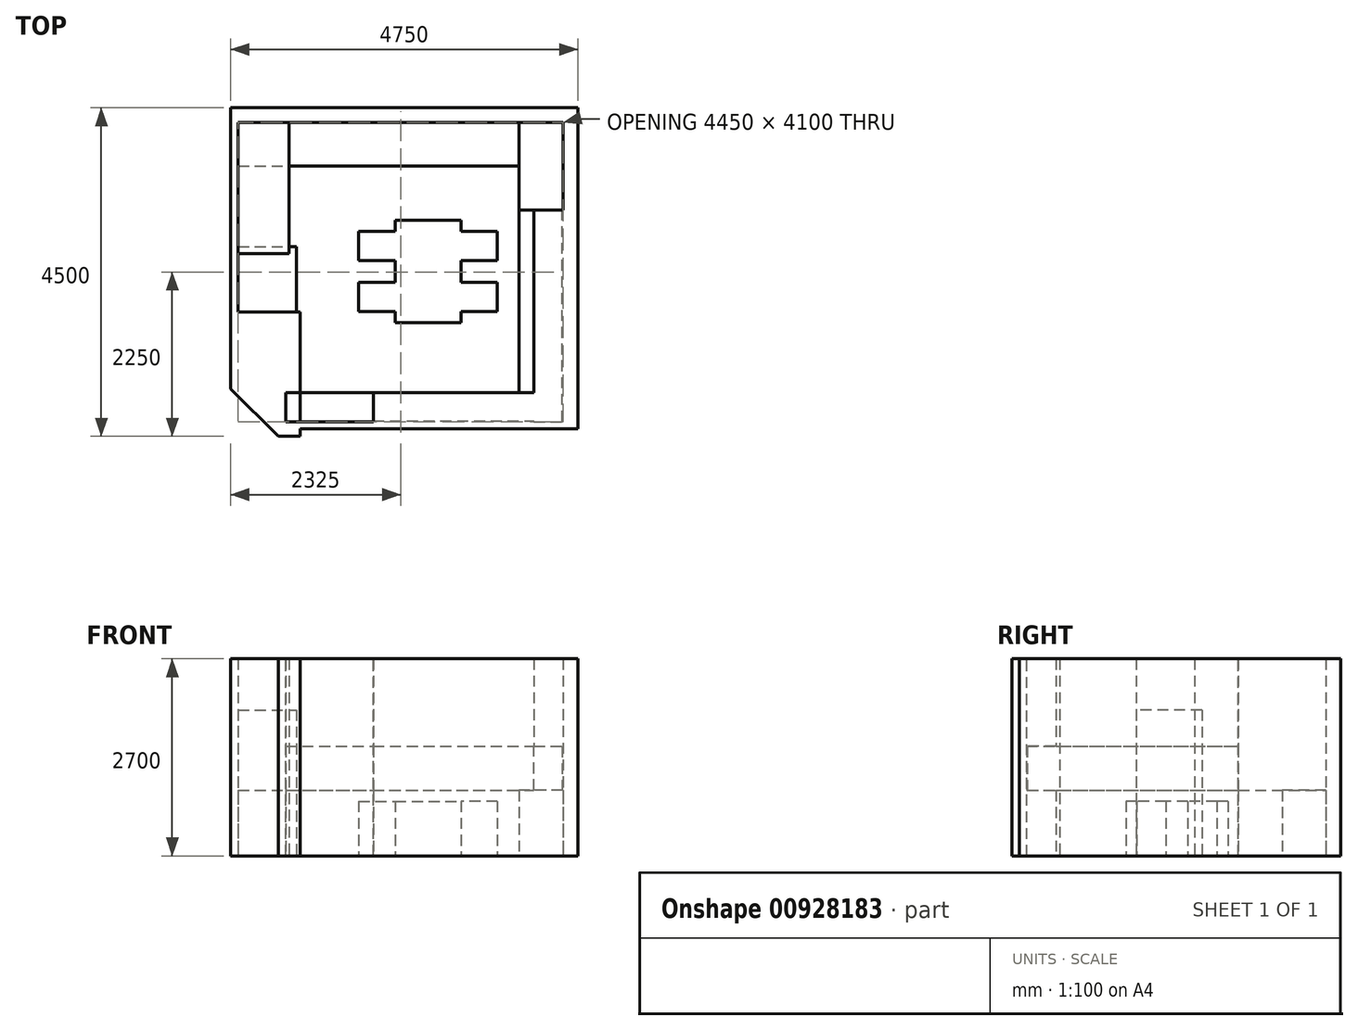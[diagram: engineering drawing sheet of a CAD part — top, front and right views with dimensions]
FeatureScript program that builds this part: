
annotation { "Feature Type Name" : "Feature", "Feature Type Description" : "" }
export const myFeature = defineFeature(function(context is Context, id is Id, definition is map)
    precondition{}
    {
        {
            var Q0;
            Q0=qCreatedBy(makeId("Top.planeOp"),FACE);
            var sketch = newSketch(context, id + "F0", { "sketchPlane" : qUnion([Q0])});
            skLineSegment(sketch, "E0", {"start": v(-2225, 1641.97) * mm, "end": v(2225, 1641.97) * mm});
            skLineSegment(sketch, "E1", {"start": v(2225, 1641.97) * mm, "end": v(2225, -2458.03) * mm});
            skLineSegment(sketch, "E2", {"start": v(-2225, -958.03) * mm, "end": v(-2225, 1641.97) * mm});
            skLineSegment(sketch, "E3.bottom", {"start": v(-2325, 1841.97) * mm, "end": v(2425, 1841.97) * mm});
            skLineSegment(sketch, "E3.left", {"start": v(-2325, 1841.97) * mm, "end": v(-2325, -2008.03) * mm});
            skLineSegment(sketch, "E3.right", {"start": v(2425, 1841.97) * mm, "end": v(2425, -2558.03) * mm});
            skLineSegment(sketch, "E4", {"start": v(-2225, -958.03) * mm, "end": v(-1375, -958.03) * mm});
            skLineSegment(sketch, "E5", {"start": v(-1375, -958.03) * mm, "end": v(-1375, -2658.03) * mm});
            skLineSegment(sketch, "E6", {"start": v(-2325, -2008.03) * mm, "end": v(-1675, -2658.03) * mm});
            skLineSegment(sketch, "E7", {"start": v(-1375, -2658.03) * mm, "end": v(-1675, -2658.03) * mm});
            skLineSegment(sketch, "E8", {"start": v(2425, -2558.03) * mm, "end": v(-1375, -2558.03) * mm});
            skLineSegment(sketch, "E9", {"start": v(2225, -2458.03) * mm, "end": v(-1375, -2458.03) * mm});
            skSolve(sketch);
        }
        {
            var Q0;
            Q0=makeQuery(id+"F0.imprint","IMPRINT",FACE,{"disambiguationData":[TD([[makeQuery(id+"F0.imprint","IMPRINT",EDGE,{"derivedFrom":sQuery(id+"F0.wireOp",EDGE,"E0")}),1.0]])]});
            extrude(context, id + "F1", {"entities" : qUnion([Q0]), "depth" : 2700 * mm, "offsetDistance" : 25 * mm});
        }
        {
            var Q0;
            Q0=makeQuery(id+"F1.opExtrude","SWEPT_FACE",FACE,{"disambiguationData":[OSD([sQuery(id+"F0.wireOp",EDGE,"E0")])]});
            var sketch = newSketch(context, id + "F2", { "sketchPlane" : qUnion([Q0])});
            skLineSegment(sketch, "E10", {"start": v(-2225, 2700) * mm, "end": v(-1525, 2700) * mm});
            skLineSegment(sketch, "E11", {"start": v(-1525, 2700) * mm, "end": v(-1525, 0) * mm});
            skLineSegment(sketch, "E12", {"start": v(-1525, 0) * mm, "end": v(-2225, 0) * mm});
            skLineSegment(sketch, "E13", {"start": v(-2225, 0) * mm, "end": v(-2225, 2700) * mm});
            skSolve(sketch);
        }
        {
            var Q0;
            Q0=makeQuery(id+"F2.imprint","IMPRINT",FACE,{"disambiguationData":[TD([[makeQuery(id+"F2.imprint","IMPRINT",EDGE,{"derivedFrom":sQuery(id+"F2.wireOp",EDGE,"E10")}),-1.0]])]});
            extrude(context, id + "F3", {"entities" : qUnion([Q0]), "depth" : 1800 * mm, "offsetDistance" : 25 * mm});
        }
        {
            var Q0;
            Q0=qCreatedBy(makeId("Top.planeOp"),FACE);
            var sketch = newSketch(context, id + "F4", { "sketchPlane" : qUnion([Q0])});
            skLineSegment(sketch, "E14.bottom", {"start": v(-75, 300) * mm, "end": v(825, 300) * mm});
            skLineSegment(sketch, "E14.left", {"start": v(-75, 300) * mm, "end": v(-75, -1100) * mm});
            skLineSegment(sketch, "E14.right", {"start": v(825, 300) * mm, "end": v(825, -1100) * mm});
            skLineSegment(sketch, "E15", {"start": v(-75, -1100) * mm, "end": v(825, -1100) * mm});
            skLineSegment(sketch, "E16", {"start": v(-75, 150) * mm, "end": v(-575, 150) * mm});
            skLineSegment(sketch, "E17", {"start": v(-575, 150) * mm, "end": v(-575, -250) * mm});
            skLineSegment(sketch, "E18", {"start": v(-575, -250) * mm, "end": v(-75, -250) * mm});
            skLineSegment(sketch, "E19", {"start": v(-75, -550) * mm, "end": v(-575, -550) * mm});
            skLineSegment(sketch, "E20", {"start": v(-575, -550) * mm, "end": v(-575, -950) * mm});
            skLineSegment(sketch, "E21", {"start": v(-575, -950) * mm, "end": v(-75, -950) * mm});
            skLineSegment(sketch, "E22", {"start": v(825, 150) * mm, "end": v(1325, 150) * mm});
            skLineSegment(sketch, "E23", {"start": v(1325, 150) * mm, "end": v(1325, -250) * mm});
            skLineSegment(sketch, "E24", {"start": v(1325, -250) * mm, "end": v(825, -250) * mm});
            skLineSegment(sketch, "E25", {"start": v(825, -550) * mm, "end": v(1325, -550) * mm});
            skLineSegment(sketch, "E26", {"start": v(1325, -550) * mm, "end": v(1325, -950) * mm});
            skLineSegment(sketch, "E27", {"start": v(1325, -950) * mm, "end": v(825, -950) * mm});
            skLineSegment(sketch, "E28", {"start": v(-75, -400) * mm, "end": v(825, -400) * mm});
            skSolve(sketch);
        }
        {
            var Q0;
            {var subQ0=sQuery(id+"F4.wireOp",EDGE,"E16");Q0=makeQuery(id+"F4.imprint","IMPRINT",FACE,{"disambiguationData":[TD([[makeQuery(id+"F4.imprint","IMPRINT",EDGE,{"derivedFrom":subQ0}),1.0]])]});}
            var Q1;
            {var subQ4=sQuery(id+"F4.wireOp",EDGE,"E14.bottom");Q1=makeQuery(id+"F4.imprint","IMPRINT",FACE,{"disambiguationData":[TD([[makeQuery(id+"F4.imprint","IMPRINT",EDGE,{"derivedFrom":subQ4}),-1.0]])]});}
            var Q2;
            {var subQ0=sQuery(id+"F4.wireOp",EDGE,"E22");Q2=makeQuery(id+"F4.imprint","IMPRINT",FACE,{"disambiguationData":[TD([[makeQuery(id+"F4.imprint","IMPRINT",EDGE,{"derivedFrom":subQ0}),-1.0]])]});}
            var Q3;
            {var subQ0=sQuery(id+"F4.wireOp",EDGE,"E15");Q3=makeQuery(id+"F4.imprint","IMPRINT",FACE,{"disambiguationData":[TD([[makeQuery(id+"F4.imprint","IMPRINT",EDGE,{"derivedFrom":subQ0}),1.0]])]});}
            var Q4;
            {var subQ0=sQuery(id+"F4.wireOp",EDGE,"E19");Q4=makeQuery(id+"F4.imprint","IMPRINT",FACE,{"disambiguationData":[TD([[makeQuery(id+"F4.imprint","IMPRINT",EDGE,{"derivedFrom":subQ0}),1.0]])]});}
            var Q5;
            {var subQ0=sQuery(id+"F4.wireOp",EDGE,"E25");Q5=makeQuery(id+"F4.imprint","IMPRINT",FACE,{"disambiguationData":[TD([[makeQuery(id+"F4.imprint","IMPRINT",EDGE,{"derivedFrom":subQ0}),-1.0]])]});}
            extrude(context, id + "F5", {"entities" : qUnion([Q0, Q1, Q2, Q3, Q4, Q5]), "depth" : 750 * mm, "offsetDistance" : 25 * mm});
        }
        {
            var Q0;
            Q0=makeQuery(id+"F1.opExtrude","SWEPT_FACE",FACE,{"disambiguationData":[OSD([sQuery(id+"F0.wireOp",EDGE,"E0")])]});
            var sketch = newSketch(context, id + "F6", { "sketchPlane" : qUnion([Q0])});
            skLineSegment(sketch, "E29.bottom", {"start": v(2225, 900) * mm, "end": v(1625, 900) * mm});
            skLineSegment(sketch, "E29.top", {"start": v(2225, 0) * mm, "end": v(1625, 0) * mm});
            skLineSegment(sketch, "E29.left", {"start": v(2225, 900) * mm, "end": v(2225, 0) * mm});
            skLineSegment(sketch, "E29.right", {"start": v(1625, 900) * mm, "end": v(1625, 0) * mm});
            skSolve(sketch);
        }
        {
            var Q0;
            Q0=makeQuery(id+"F6.imprint","IMPRINT",FACE,{"disambiguationData":[TD([[makeQuery(id+"F6.imprint","IMPRINT",EDGE,{"derivedFrom":sQuery(id+"F6.wireOp",EDGE,"E29.bottom")}),1.0]])]});
            extrude(context, id + "F7", {"entities" : qUnion([Q0]), "depth" : 1200 * mm, "offsetDistance" : 25 * mm});
        }
        {
            var Q0;
            Q0=makeQuery(id+"F7.opExtrude","CAP_FACE",FACE,{"disambiguationData":[OSD([sQuery(id+"F6.wireOp",EDGE,"E29.bottom"),sQuery(id+"F6.wireOp",EDGE,"E29.top"),sQuery(id+"F6.wireOp",EDGE,"E29.left"),sQuery(id+"F6.wireOp",EDGE,"E29.right")])],"isStart":false});
            var sketch = newSketch(context, id + "F8", { "sketchPlane" : qUnion([Q0])});
            skLineSegment(sketch, "E30", {"start": v(2225, 0) * mm, "end": v(2225, 2700) * mm});
            skLineSegment(sketch, "E31", {"start": v(2225, 2700) * mm, "end": v(1825, 2700) * mm});
            skLineSegment(sketch, "E32", {"start": v(1825, 2700) * mm, "end": v(1825, 1500) * mm});
            skLineSegment(sketch, "E33", {"start": v(1825, 1500) * mm, "end": v(2215, 1500) * mm});
            skLineSegment(sketch, "E34", {"start": v(2215, 1500) * mm, "end": v(2215, 900) * mm});
            skLineSegment(sketch, "E35", {"start": v(2215, 900) * mm, "end": v(1625, 900) * mm});
            skLineSegment(sketch, "E36", {"start": v(1625, 900) * mm, "end": v(1625, 0) * mm});
            skLineSegment(sketch, "E37", {"start": v(1625, 0) * mm, "end": v(2225, 0) * mm});
            skSolve(sketch);
        }
        {
            var Q0;
            {var subQ0=sQuery(id+"F8.wireOp",EDGE,"E31");Q0=makeQuery(id+"F8.imprint","IMPRINT",FACE,{"disambiguationData":[TD([[makeQuery(id+"F8.imprint","IMPRINT",EDGE,{"derivedFrom":subQ0}),1.0]])]});}
            var Q1;
            {var subQ1=sQuery(id+"F8.wireOp",EDGE,"E35");Q1=makeQuery(id+"F8.imprint","IMPRINT",FACE,{"disambiguationData":[TD([[makeQuery(id+"F8.imprint","IMPRINT",EDGE,{"derivedFrom":subQ1}),1.0]])]});}
            extrude(context, id + "F9", {"entities" : qUnion([Q0, Q1]), "endBound" : BoundingType.UP_TO_NEXT, "depth" : 25 * mm, "offsetDistance" : 25 * mm});
        }
        {
            var Q0;
            Q0=makeQuery(id+"F9.opExtrude","SWEPT_FACE",FACE,{"disambiguationData":[OSD([sQuery(id+"F8.wireOp",EDGE,"E36")])]});
            var sketch = newSketch(context, id + "F10", { "sketchPlane" : qUnion([Q0])});
            skLineSegment(sketch, "E38", {"start": v(2458.03, 0) * mm, "end": v(2458.03, 2700) * mm});
            skLineSegment(sketch, "E39", {"start": v(2458.03, 2700) * mm, "end": v(2058.03, 2700) * mm});
            skLineSegment(sketch, "E40", {"start": v(2058.03, 2700) * mm, "end": v(2058.03, 1500) * mm});
            skLineSegment(sketch, "E41", {"start": v(2058.03, 1500) * mm, "end": v(2448.03, 1500) * mm});
            skLineSegment(sketch, "E42", {"start": v(2448.03, 1500) * mm, "end": v(2448.03, 900) * mm});
            skLineSegment(sketch, "E43", {"start": v(2448.03, 900) * mm, "end": v(2058.03, 900) * mm});
            skLineSegment(sketch, "E44", {"start": v(2058.03, 900) * mm, "end": v(2058.03, 0) * mm});
            skLineSegment(sketch, "E45", {"start": v(2058.03, 0) * mm, "end": v(2458.03, 0) * mm});
            skSolve(sketch);
        }
        {
            var Q0;
            {var subQ0=sQuery(id+"F10.wireOp",EDGE,"E39");Q0=makeQuery(id+"F10.imprint","IMPRINT",FACE,{"disambiguationData":[TD([[makeQuery(id+"F10.imprint","IMPRINT",EDGE,{"derivedFrom":subQ0}),1.0]])]});}
            var Q1;
            {var subQ1=sQuery(id+"F10.wireOp",EDGE,"E43");Q1=makeQuery(id+"F10.imprint","IMPRINT",FACE,{"disambiguationData":[TD([[makeQuery(id+"F10.imprint","IMPRINT",EDGE,{"derivedFrom":subQ1}),1.0]])]});}
            extrude(context, id + "F11", {"entities" : qUnion([Q0, Q1]), "operationType" : NewBodyOperationType.ADD, "depth" : 2000 * mm, "offsetDistance" : 25 * mm, "hasSecondDirection" : true, "secondDirectionOppositeDirection" : true, "secondDirectionDepth" : 200 * mm});
        }
        {
            var Q0;
            Q0=makeQuery(id+"F11.opExtrude","CAP_FACE",FACE,{"disambiguationData":[OSD([sQuery(id+"F10.wireOp",EDGE,"E38"),sQuery(id+"F10.wireOp",EDGE,"E39"),sQuery(id+"F10.wireOp",EDGE,"E40"),sQuery(id+"F10.wireOp",EDGE,"E41"),sQuery(id+"F10.wireOp",EDGE,"E42"),sQuery(id+"F10.wireOp",EDGE,"E43"),sQuery(id+"F10.wireOp",EDGE,"E44"),sQuery(id+"F10.wireOp",EDGE,"E45")])],"isStart":false});
            var sketch = newSketch(context, id + "F12", { "sketchPlane" : qUnion([Q0])});
            skLineSegment(sketch, "E46.bottom", {"start": v(2458.03, 2700) * mm, "end": v(2058.03, 2700) * mm});
            skLineSegment(sketch, "E46.top", {"start": v(2458.03, 0) * mm, "end": v(2058.03, 0) * mm});
            skLineSegment(sketch, "E46.left", {"start": v(2458.03, 2700) * mm, "end": v(2458.03, 0) * mm});
            skLineSegment(sketch, "E46.right", {"start": v(2058.03, 2700) * mm, "end": v(2058.03, 0) * mm});
            skSolve(sketch);
        }
        {
            var Q0;
            {var subQ4=makeQuery(id+"F11.opExtrude","CAP_EDGE",EDGE,{"disambiguationData":[OSD([sQuery(id+"F10.wireOp",EDGE,"E40")])],"isStart":false});Q0=makeQuery(id+"F12.imprint","IMPRINT",FACE,{"disambiguationData":[TD([[makeQuery(id+"F12.imprint","IMPRINT",EDGE,{"derivedFrom":subQ4}),-1.0]])]});}
            var Q1;
            {var subQ1=sQuery(id+"F12.wireOp",EDGE,"E46.top");Q1=makeQuery(id+"F12.imprint","IMPRINT",FACE,{"disambiguationData":[TD([[makeQuery(id+"F12.imprint","IMPRINT",EDGE,{"derivedFrom":subQ1}),-1.0]])]});}
            extrude(context, id + "F13", {"entities" : qUnion([Q0, Q1]), "depth" : 1200 * mm, "offsetDistance" : 25 * mm});
        }
        {
            var Q0;
            Q0=qCreatedBy(makeId("Top.planeOp"),FACE);
            var sketch = newSketch(context, id + "F14", { "sketchPlane" : qUnion([Q0])});
            skLineSegment(sketch, "E47.bottom", {"start": v(-2225, -58.03) * mm, "end": v(-1425, -58.03) * mm});
            skLineSegment(sketch, "E47.top", {"start": v(-2225, -958.03) * mm, "end": v(-1425, -958.03) * mm});
            skLineSegment(sketch, "E47.left", {"start": v(-2225, -58.03) * mm, "end": v(-2225, -958.03) * mm});
            skLineSegment(sketch, "E47.right", {"start": v(-1425, -58.03) * mm, "end": v(-1425, -958.03) * mm});
            skLineSegment(sketch, "E48.bottom", {"start": v(-2225, 1641.97) * mm, "end": v(1625, 1641.97) * mm});
            skLineSegment(sketch, "E48.top", {"start": v(-2225, 1041.97) * mm, "end": v(1625, 1041.97) * mm});
            skLineSegment(sketch, "E48.left", {"start": v(-2225, 1641.97) * mm, "end": v(-2225, 1041.97) * mm});
            skLineSegment(sketch, "E48.right", {"start": v(1625, 1641.97) * mm, "end": v(1625, 1041.97) * mm});
            skSolve(sketch);
        }
        {
            var Q0;
            Q0=makeQuery(id+"F14.imprint","IMPRINT",FACE,{"disambiguationData":[TD([[makeQuery(id+"F14.imprint","IMPRINT",EDGE,{"derivedFrom":sQuery(id+"F14.wireOp",EDGE,"E48.bottom")}),-1.0]])]});
            extrude(context, id + "F15", {"entities" : qUnion([Q0]), "depth" : 900 * mm, "offsetDistance" : 25 * mm});
        }
        {
            var Q0;
            Q0=makeQuery(id+"F14.imprint","IMPRINT",FACE,{"disambiguationData":[TD([[makeQuery(id+"F14.imprint","IMPRINT",EDGE,{"derivedFrom":sQuery(id+"F14.wireOp",EDGE,"E47.bottom")}),-1.0]])]});
            extrude(context, id + "F16", {"entities" : qUnion([Q0]), "depth" : 2000 * mm, "offsetDistance" : 25 * mm});
        }
    });
